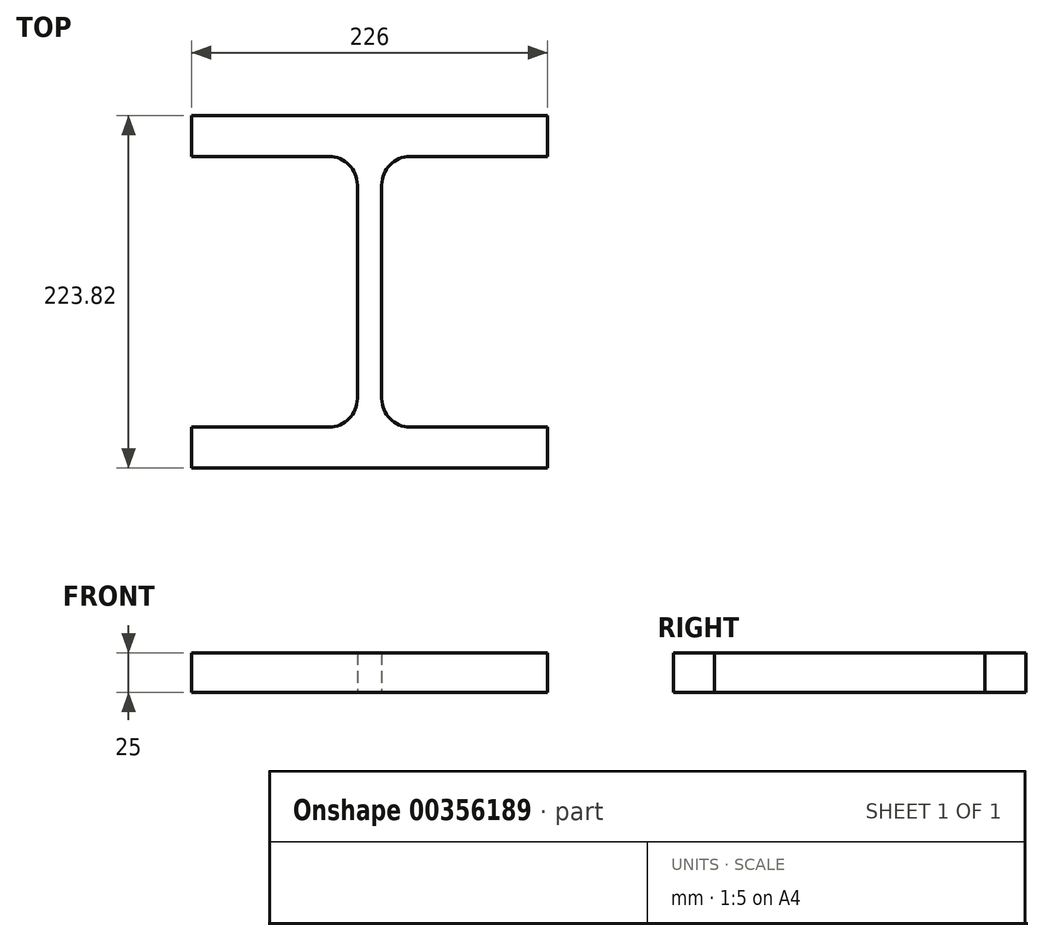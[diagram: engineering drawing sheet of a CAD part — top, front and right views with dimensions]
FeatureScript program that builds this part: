
annotation { "Feature Type Name" : "Feature", "Feature Type Description" : "" }
export const myFeature = defineFeature(function(context is Context, id is Id, definition is map)
    precondition{}
    {
        {
            var Q0;
            Q0=qCreatedBy(makeId("Top.planeOp"),FACE);
            var sketch = newSketch(context, id + "F0", { "sketchPlane" : qUnion([Q0])});
            skLineSegment(sketch, "E0", {"start": v(-127.4, 117.7) * mm, "end": v(98.6, 117.7) * mm});
            skLineSegment(sketch, "E1", {"start": v(98.6, 117.7) * mm, "end": v(98.6, 91.7) * mm});
            skLineSegment(sketch, "E2", {"start": v(98.6, 91.7) * mm, "end": v(11.34, 91.7) * mm});
            skLineSegment(sketch, "E3", {"start": v(-6.66, 73.7) * mm, "end": v(-6.66, -62.12) * mm});
            skLineSegment(sketch, "E4", {"start": v(11.34, -80.12) * mm, "end": v(98.6, -80.12) * mm});
            skLineSegment(sketch, "E5", {"start": v(98.6, -80.12) * mm, "end": v(98.6, -106.12) * mm});
            skLineSegment(sketch, "E6", {"start": v(98.6, -106.12) * mm, "end": v(-127.4, -106.12) * mm});
            skLineSegment(sketch, "E7", {"start": v(-127.4, -106.12) * mm, "end": v(-127.4, -80.12) * mm});
            skLineSegment(sketch, "E8", {"start": v(-127.4, -80.12) * mm, "end": v(-40.16, -80.12) * mm});
            skLineSegment(sketch, "E9", {"start": v(-22.16, -62.12) * mm, "end": v(-22.16, 73.7) * mm});
            skLineSegment(sketch, "E10", {"start": v(-40.16, 91.7) * mm, "end": v(-127.4, 91.7) * mm});
            skLineSegment(sketch, "E11", {"start": v(-127.4, 91.7) * mm, "end": v(-127.4, 117.7) * mm});
            skPoint(sketch, "E12.visualSharp", {"position": v(-22.16, 91.7) * mm});
            skArc(sketch, "E12.filletArc", {"start": v(-22.16, 73.7) * mm, "mid": v(-27.43, 86.42) * mm, "end": v(-40.16, 91.7) * mm});
            skPoint(sketch, "E13.visualSharp", {"position": v(-6.66, 91.7) * mm});
            skArc(sketch, "E13.filletArc", {"start": v(11.34, 91.7) * mm, "mid": v(-1.39, 86.42) * mm, "end": v(-6.66, 73.7) * mm});
            skPoint(sketch, "E14.visualSharp", {"position": v(-22.16, -80.12) * mm});
            skArc(sketch, "E14.filletArc", {"start": v(-40.16, -80.12) * mm, "mid": v(-27.43, -74.85) * mm, "end": v(-22.16, -62.12) * mm});
            skPoint(sketch, "E15.visualSharp", {"position": v(-6.66, -80.12) * mm});
            skArc(sketch, "E15.filletArc", {"start": v(-6.66, -62.12) * mm, "mid": v(-1.39, -74.85) * mm, "end": v(11.34, -80.12) * mm});
            skSolve(sketch);
        }
        {
            var Q0;
            Q0=makeQuery(id+"F0.imprint","IMPRINT",FACE,{"disambiguationData":[TD([[makeQuery(id+"F0.imprint","IMPRINT",EDGE,{"derivedFrom":sQuery(id+"F0.wireOp",EDGE,"E0")}),-1.0]])]});
            extrude(context, id + "F1", {"entities" : qUnion([Q0]), "depth" : 25 * mm});
        }
    });
